FCSTD DOCUMENT  (FreeCAD 0.19R23578 (Git))
Label: reel_interrupter_clip
License: All rights reserved
LicenseURL: http://en.wikipedia.org/wiki/All_rights_reserved
objects: Sketcher::SketchObject×1, PartDesign::Body×1
note: 2 computed .brp shape members not serialized (recipe doc carries the construction recipe); baked Part::Feature solids carry a one-line shape summary decoded from their .brp

FEATURE [Sketcher::SketchObject] Sketch
  MapMode = 5
  Support = -> [XY_Plane]
  sketch-geometry (7):
    g0: LineSegment StartX=0 StartY=0 StartZ=0 EndX=13 EndY=0 EndZ=0
    g1: LineSegment StartX=4 StartY=0 StartZ=0 EndX=4 EndY=13 EndZ=0
    g2: LineSegment StartX=13 StartY=0 StartZ=0 EndX=13 EndY=10 EndZ=0
    g3: LineSegment StartX=13 StartY=10 StartZ=0 EndX=22 EndY=10 EndZ=0
    g4: ArcOfCircle CenterX=20.5 CenterY=10 CenterZ=0 NormalX=0 NormalY=0 NormalZ=1 AngleXU=0 Radius=1.5 StartAngle=6e-16 EndAngle=3.14159
    g5: ArcOfCircle CenterX=16 CenterY=10 CenterZ=0 NormalX=0 NormalY=0 NormalZ=1 AngleXU=0 Radius=0.5 StartAngle=3.14159 EndAngle=6.28319
    g6: ArcOfCircle CenterX=13 CenterY=7 CenterZ=0 NormalX=0 NormalY=0 NormalZ=1 AngleXU=0 Radius=0.5 StartAngle=4.71241 EndAngle=7.85396
  constraints (27):
    c: Coincident(g0,g-1)
    c: PointOnObject(g0,g-1)
    c: DistanceX(g0,g0) = 13
    c: PointOnObject(g1,g0)
    c: Vertical(g1)
    c: DistanceX(g1,g0) = 9
    c: DistanceY(g1,g1) = 13
    c: Coincident(g2,g0)
    c: Vertical(g2)
    c: Horizontal(g3)
    c: PointOnObject(g4,g3)
    c: Diameter(g4) = 3
    c: Coincident(g4,g3)
    c: PointOnObject(g4,g3)
    c: DistanceX(g3,g3) = 9
    c: DistanceY(g2,g2) = 10
    c: Coincident(g3,g2)
    c: Diameter(g5) = 1
    c: DistanceX(g2,g5) = 3
    c: DistanceY(g5,g5) = 0
    c: DistanceY(g5,g5) = 0
    c: PointOnObject(g5,g3)
    c: Diameter(g6) = 1
    c: DistanceY(g6,g6) = 0.5
    c: DistanceY(g6,g6) = 0.5
    c: DistanceY(g6,g2) = 3
    c: DistanceX(g2,g6) = 0
FEATURE [PartDesign::Body] Body
  Group = -> [Sketch]
  Origin = -> Origin
